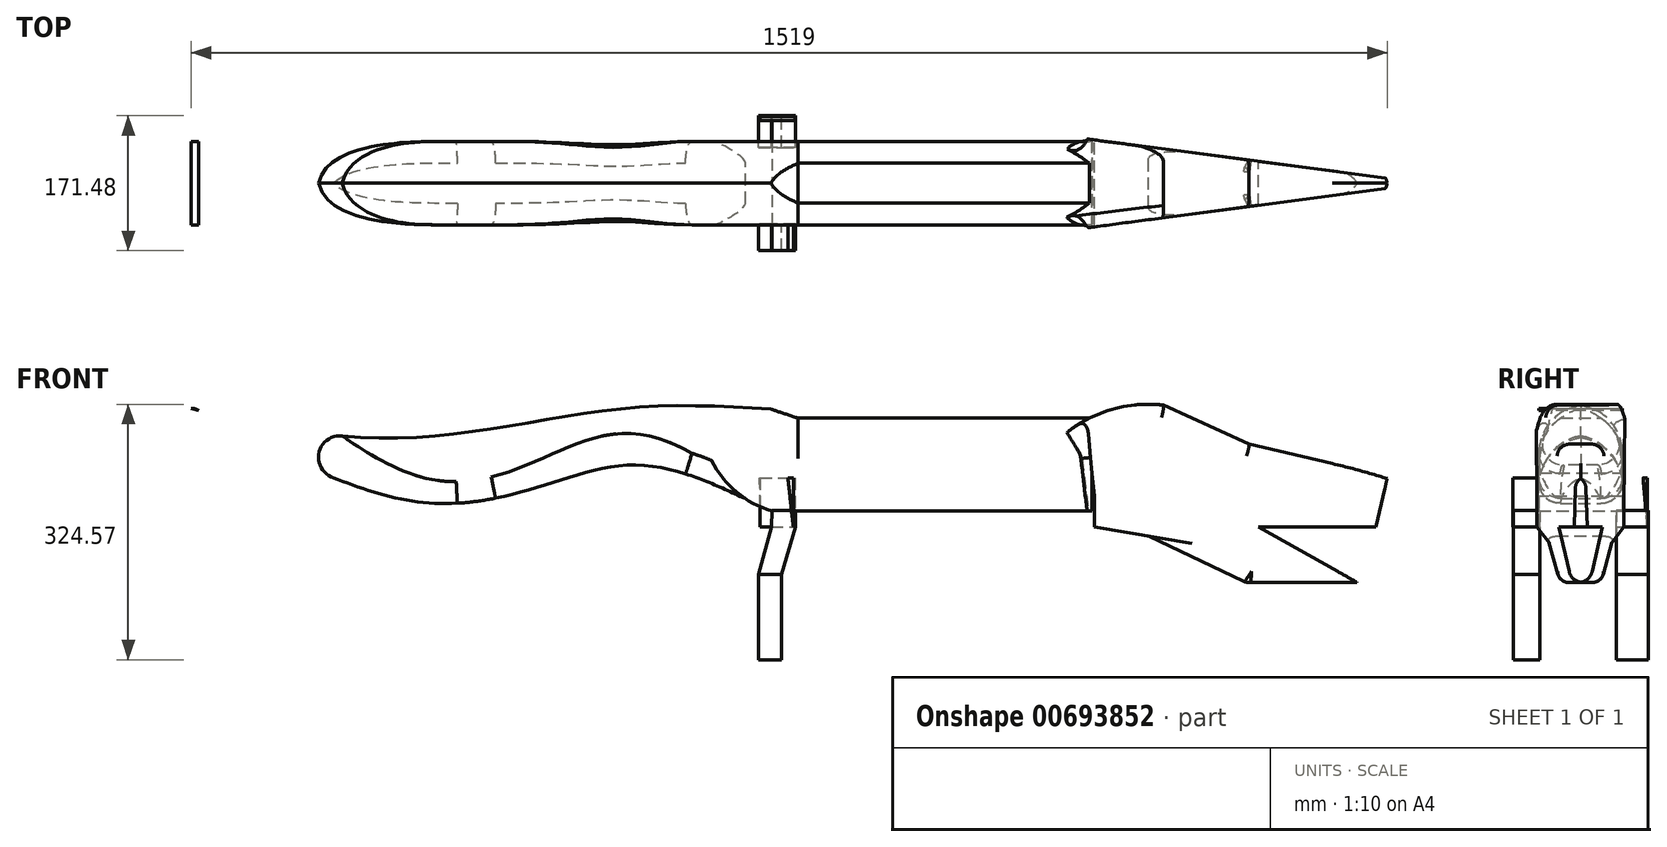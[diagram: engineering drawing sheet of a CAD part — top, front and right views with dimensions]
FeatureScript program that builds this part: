
annotation { "Feature Type Name" : "Feature", "Feature Type Description" : "" }
export const myFeature = defineFeature(function(context is Context, id is Id, definition is map)
    precondition{}
    {
        {
            var Q0;
            Q0=qCreatedBy(makeId("Front.planeOp"),FACE);
            var sketch = newSketch(context, id + "F0", { "sketchPlane" : qUnion([Q0])});
            skLineSegment(sketch, "E0", {"start": v(-53.86, 0) * mm, "end": v(-70.14, -60.07) * mm});
            skLineSegment(sketch, "E1", {"start": v(-70.14, -60.07) * mm, "end": v(-40.72, -60.07) * mm});
            skLineSegment(sketch, "E2", {"start": v(-40.72, -60.07) * mm, "end": v(-23.4, 0) * mm});
            skLineSegment(sketch, "E3", {"start": v(-23.4, 0) * mm, "end": v(27.61, 0) * mm});
            skLineSegment(sketch, "E4", {"start": v(27.61, 0) * mm, "end": v(27.61, -61.63) * mm});
            skLineSegment(sketch, "E5", {"start": v(27.61, -61.63) * mm, "end": v(54.41, -61.63) * mm});
            skLineSegment(sketch, "E6", {"start": v(54.41, -61.63) * mm, "end": v(55.43, 0) * mm});
            skLineSegment(sketch, "E7", {"start": v(55.43, 0) * mm, "end": v(55.8, 22.02) * mm});
            skLineSegment(sketch, "E8", {"start": v(55.8, 22.02) * mm, "end": v(-52.85, 21.34) * mm});
            skLineSegment(sketch, "E9", {"start": v(-52.85, 21.34) * mm, "end": v(-53.86, 0) * mm});
            skSolve(sketch);
        }
        {
            var Q0;
            Q0 = qSketchRegion(id + "F0", true);
            extrude(context, id + "F1", {"entities" : qUnion([Q0]), "endBound" : BoundingType.SYMMETRIC, "depth" : 171.23 * mm, "offsetDistance" : 25.4 * mm});
        }
        {
            var Q0;
            Q0=qCreatedBy(makeId("Right.planeOp"),FACE);
            var sketch = newSketch(context, id + "F2", { "sketchPlane" : qUnion([Q0])});
            skLineSegment(sketch, "E10.bottom", {"start": v(-51.76, 31.02) * mm, "end": v(45.2, 31.02) * mm});
            skLineSegment(sketch, "E10.top", {"start": v(-51.76, -73.58) * mm, "end": v(45.2, -73.58) * mm});
            skLineSegment(sketch, "E10.left", {"start": v(-51.76, 31.02) * mm, "end": v(-51.76, -73.58) * mm});
            skLineSegment(sketch, "E10.right", {"start": v(45.2, 31.02) * mm, "end": v(45.2, -73.58) * mm});
            skSolve(sketch);
        }
        {
            var Q0;
            Q0 = qSketchRegion(id + "F2", true);
            extrude(context, id + "F3", {"entities" : qUnion([Q0]), "operationType" : NewBodyOperationType.REMOVE, "endBound" : BoundingType.SYMMETRIC, "oppositeDirection" : true, "depth" : 377.92 * mm, "offsetDistance" : 25.4 * mm});
        }
        {
            var Q0;
            Q0=qCreatedBy(makeId("Front.planeOp"),FACE);
            var sketch = newSketch(context, id + "F4", { "sketchPlane" : qUnion([Q0])});
            skLineSegment(sketch, "E11.bottom", {"start": v(-23.26, 23.35) * mm, "end": v(61.77, 23.35) * mm});
            skLineSegment(sketch, "E11.top", {"start": v(-23.26, -66.33) * mm, "end": v(61.77, -66.33) * mm});
            skLineSegment(sketch, "E11.left", {"start": v(-23.26, 23.35) * mm, "end": v(-23.26, -66.33) * mm});
            skLineSegment(sketch, "E11.right", {"start": v(61.77, 23.35) * mm, "end": v(61.77, -66.33) * mm});
            skSolve(sketch);
        }
        {
            var Q0;
            Q0=makeQuery(id+"F4.imprint","IMPRINT",FACE,{"disambiguationData":[TD([[makeQuery(id+"F4.imprint","IMPRINT",EDGE,{"derivedFrom":sQuery(id+"F4.wireOp",EDGE,"E11.bottom")}),-1.0]])]});
            extrude(context, id + "F5", {"entities" : qUnion([Q0]), "operationType" : NewBodyOperationType.REMOVE, "endBound" : BoundingType.SYMMETRIC, "depth" : 666.9 * mm, "offsetDistance" : 25.4 * mm});
        }
        {
            var Q0;
            Q0=makeQuery(id+"F4.imprint","IMPRINT",FACE,{"disambiguationData":[TD([[makeQuery(id+"F4.imprint","IMPRINT",EDGE,{"derivedFrom":sQuery(id+"F4.wireOp",EDGE,"E11.bottom")}),-1.0]])]});
            extrude(context, id + "F6", {"entities" : qUnion([Q0]), "operationType" : NewBodyOperationType.REMOVE, "depth" : 410.42 * mm, "offsetDistance" : 25.4 * mm});
        }
        {
            var Q0;
            Q0=qCreatedBy(makeId("Front.planeOp"),FACE);
            var sketch = newSketch(context, id + "F7", { "sketchPlane" : qUnion([Q0])});
            skFitSpline(sketch, "E12", {"points": [v(-86.96, 36.28) * mm, v(-245.8, 78.26) * mm, v(-505.62, 32.65) * mm, v(-786.2, 150.55) * mm, v(-790.65, 150.56) * mm], "startDerivative": vector(-580.58, 269.58) * mm, "endDerivative": vector(-61.42, -29.2) * mm});
            skFitSpline(sketch, "E13", {"points": [v(-790.65, 150.56) * mm, v(-523.28, 113.86) * mm, v(-248.53, 150.56) * mm, v(-56.26, 150.56) * mm], "startDerivative": vector(752.16, -167.95) * mm, "endDerivative": vector(620.07, -38.03) * mm});
            skArc(sketch, "E14", {"start": v(-86.96, 36.28) * mm, "mid": v(-70.22, 27.1) * mm, "end": v(-52.25, 20.62) * mm});
            skLineSegment(sketch, "E15", {"start": v(-56.26, 150.56) * mm, "end": v(-19.94, 138.54) * mm});
            skLineSegment(sketch, "E16", {"start": v(-19.94, 20.62) * mm, "end": v(-19.94, 138.54) * mm});
            skLineSegment(sketch, "E17", {"start": v(-52.25, 20.62) * mm, "end": v(-19.94, 20.62) * mm});
            skSolve(sketch);
        }
        {
            var Q0;
            Q0 = qSketchRegion(id + "F7", true);
            extrude(context, id + "F8", {"entities" : qUnion([Q0]), "endBound" : BoundingType.SYMMETRIC, "depth" : 106.25 * mm, "offsetDistance" : 25.4 * mm});
        }
        {
            var Q0;
            {var subQ0=sQuery(id+"F7.wireOp",EDGE,"E13");Q0=makeQuery(id+"F8.opExtrude","CAP_EDGE",EDGE,{"disambiguationData":[OSD([subQ0]),TDD([makeQuery(id+"F7.imprint","IMPRINT",EDGE,{"disambiguationData":[TD([[makeQuery(id+"F7.imprint","INTERSECT",VERTEX,{"derivedFrom":[subQ0,sQuery(id+"F7.wireOp",EDGE,"E15")]}),1.0]])],"derivedFrom":subQ0})])],"isStart":false});}
            var Q1;
            {var subQ0=sQuery(id+"F7.wireOp",EDGE,"E13");Q1=makeQuery(id+"F8.opExtrude","CAP_EDGE",EDGE,{"disambiguationData":[OSD([subQ0]),TDD([makeQuery(id+"F7.imprint","IMPRINT",EDGE,{"disambiguationData":[TD([[makeQuery(id+"F7.imprint","INTERSECT",VERTEX,{"derivedFrom":[subQ0,sQuery(id+"F7.wireOp",EDGE,"E15")]}),1.0]])],"derivedFrom":subQ0})])],"isStart":true});}
            fillet(context, id + "F9", {"entities" : qUnion([Q0, Q1]), "radius" : 61 * mm, "tangentPropagation" : true, "allowEdgeOverflow" : false});
        }
        {
            var Q0;
            {var subQ0=sQuery(id+"F7.wireOp",EDGE,"E12");Q0=makeQuery(id+"F8.opExtrude","CAP_EDGE",EDGE,{"disambiguationData":[OSD([subQ0]),TDD([makeQuery(id+"F7.imprint","IMPRINT",EDGE,{"disambiguationData":[TD([[makeQuery(id+"F7.imprint","INTERSECT",VERTEX,{"derivedFrom":[subQ0,sQuery(id+"F7.wireOp",EDGE,"E14")]}),-1.0]])],"derivedFrom":subQ0})])],"isStart":false});}
            var Q1;
            {var subQ0=sQuery(id+"F7.wireOp",EDGE,"E12");var subQ1=sQuery(id+"F7.wireOp",EDGE,"E13");Q1=makeQuery(id+"F9.opFillet","BLEND_EDGE",EDGE,{"blendedFrom":[makeQuery(id+"F8.opExtrude","CAP_EDGE",EDGE,{"disambiguationData":[OSD([subQ1]),TDD([makeQuery(id+"F7.imprint","IMPRINT",EDGE,{"disambiguationData":[TD([[makeQuery(id+"F7.imprint","INTERSECT",VERTEX,{"derivedFrom":[subQ1,sQuery(id+"F7.wireOp",EDGE,"E15")]}),1.0]])],"derivedFrom":subQ1})])],"isStart":true}),makeQuery(id+"F8.opExtrude","SWEPT_FACE",FACE,{"disambiguationData":[OSD([subQ0]),TDD([makeQuery(id+"F7.imprint","IMPRINT",EDGE,{"disambiguationData":[TD([[makeQuery(id+"F7.imprint","INTERSECT",VERTEX,{"derivedFrom":[subQ0,sQuery(id+"F7.wireOp",EDGE,"E14")]}),-1.0]])],"derivedFrom":subQ0})])]})],"blendedInto":[makeQuery(id+"F8.opExtrude","SWEPT_FACE",FACE,{"disambiguationData":[OSD([subQ0]),TDD([makeQuery(id+"F7.imprint","IMPRINT",EDGE,{"disambiguationData":[TD([[makeQuery(id+"F7.imprint","INTERSECT",VERTEX,{"derivedFrom":[subQ0,sQuery(id+"F7.wireOp",EDGE,"E14")]}),-1.0]])],"derivedFrom":subQ0})])]})]});}
            fillet(context, id + "F10", {"entities" : qUnion([Q0, Q1]), "radius" : 27.37 * mm, "tangentPropagation" : true, "allowEdgeOverflow" : false});
        }
        {
            var Q0;
            {var subQ2=sQuery(id+"F0.wireOp",EDGE,"E1");Q0=makeQuery(id+"F3.boolean.opBoolean","SPLIT",FACE,{"disambiguationData":[TD([makeQuery(id+"F3.opExtrude","SWEPT_FACE",FACE,{"disambiguationData":[OSD([sQuery(id+"F2.wireOp",EDGE,"E10.left")])]})])],"derivedFrom":makeQuery(id+"F1.opExtrude","SWEPT_FACE",FACE,{"disambiguationData":[OSD([subQ2])]})});}
            var Q1;
            {var subQ2=sQuery(id+"F0.wireOp",EDGE,"E1");Q1=makeQuery(id+"F3.boolean.opBoolean","SPLIT",FACE,{"disambiguationData":[TD([makeQuery(id+"F3.opExtrude","SWEPT_FACE",FACE,{"disambiguationData":[OSD([sQuery(id+"F2.wireOp",EDGE,"E10.right")])]})])],"derivedFrom":makeQuery(id+"F1.opExtrude","SWEPT_FACE",FACE,{"disambiguationData":[OSD([subQ2])]})});}
            extrude(context, id + "F11", {"entities" : qUnion([Q0, Q1]), "depth" : 108.32 * mm, "offsetDistance" : 25.4 * mm});
        }
        {
            var Q0;
            Q0=qCreatedBy(makeId("Top.planeOp"),FACE);
            var sketch = newSketch(context, id + "F12", { "sketchPlane" : qUnion([Q0])});
            skArc(sketch, "E18", {"start": v(-92.58, 54.35) * mm, "mid": v(-75.05, 65.13) * mm, "end": v(-68.29, 84.56) * mm});
            skArc(sketch, "E19", {"start": v(-71.39, -85.85) * mm, "mid": v(-76.16, -65.76) * mm, "end": v(-92.58, -53.25) * mm});
            skLineSegment(sketch, "E20", {"start": v(-68.29, 84.56) * mm, "end": v(-23.93, 84.56) * mm});
            skLineSegment(sketch, "E21", {"start": v(-23.93, 84.56) * mm, "end": v(-23.93, 56.67) * mm});
            skLineSegment(sketch, "E22", {"start": v(-23.93, 56.67) * mm, "end": v(-92.58, 54.35) * mm});
            skLineSegment(sketch, "E23", {"start": v(-92.58, -53.25) * mm, "end": v(-25.76, -53.25) * mm});
            skLineSegment(sketch, "E24", {"start": v(-25.76, -53.25) * mm, "end": v(-25.76, -85.87) * mm});
            skLineSegment(sketch, "E25", {"start": v(-25.76, -85.87) * mm, "end": v(-71.39, -85.85) * mm});
            skSolve(sketch);
        }
        {
            var Q0;
            Q0 = qSketchRegion(id + "F12", true);
            extrude(context, id + "F13", {"entities" : qUnion([Q0]), "depth" : 62.6 * mm, "offsetDistance" : 25.4 * mm});
        }
        {
            var Q0;
            Q0=makeQuery(id+"F8.opExtrude","SWEPT_FACE",FACE,{"disambiguationData":[OSD([sQuery(id+"F7.wireOp",EDGE,"E16")])]});
            extrude(context, id + "F14", {"entities" : qUnion([Q0]), "operationType" : NewBodyOperationType.ADD, "depth" : 373.55 * mm, "offsetDistance" : 25.4 * mm});
        }
        {
            var Q0;
            Q0=qCreatedBy(makeId("Front.planeOp"),FACE);
            var sketch = newSketch(context, id + "F15", { "sketchPlane" : qUnion([Q0])});
            skArc(sketch, "E26", {"start": v(444.04, 155.1) * mm, "mid": v(394.29, 153.32) * mm, "end": v(347.26, 137) * mm});
            skLineSegment(sketch, "E27", {"start": v(444.04, 155.1) * mm, "end": v(552.73, 105.56) * mm});
            skLineSegment(sketch, "E28", {"start": v(552.73, 105.56) * mm, "end": v(729, 64.4) * mm});
            skLineSegment(sketch, "E29", {"start": v(729, 64.4) * mm, "end": v(713.96, 0) * mm});
            skLineSegment(sketch, "E30", {"start": v(713.96, 0) * mm, "end": v(565.16, 0) * mm});
            skLineSegment(sketch, "E31", {"start": v(565.16, 0) * mm, "end": v(690.34, -70.18) * mm});
            skLineSegment(sketch, "E32", {"start": v(690.34, -70.18) * mm, "end": v(549.21, -70.18) * mm});
            skLineSegment(sketch, "E33", {"start": v(549.21, -70.18) * mm, "end": v(425.11, -11.38) * mm});
            skLineSegment(sketch, "E34", {"start": v(425.11, -11.38) * mm, "end": v(356.25, 0) * mm});
            skLineSegment(sketch, "E35", {"start": v(356.25, 0) * mm, "end": v(356.25, 39.66) * mm});
            skLineSegment(sketch, "E36", {"start": v(356.25, 39.66) * mm, "end": v(347.26, 137) * mm});
            skSolve(sketch);
        }
        {
            var Q0;
            Q0 = qSketchRegion(id + "F15", true);
            extrude(context, id + "F16", {"entities" : qUnion([Q0]), "operationType" : NewBodyOperationType.ADD, "endBound" : BoundingType.SYMMETRIC, "depth" : 139.72 * mm, "offsetDistance" : 25.4 * mm});
        }
        {
            var Q0;
            Q0=qCreatedBy(makeId("Top.planeOp"),FACE);
            var sketch = newSketch(context, id + "F17", { "sketchPlane" : qUnion([Q0])});
            skLineSegment(sketch, "E37", {"start": v(345.52, -56.98) * mm, "end": v(777.47, 0) * mm});
            skLineSegment(sketch, "E38", {"start": v(777.47, 0) * mm, "end": v(343.96, 56.5) * mm});
            skLineSegment(sketch, "E39", {"start": v(343.96, 56.5) * mm, "end": v(371.94, 271.16) * mm});
            skLineSegment(sketch, "E40", {"start": v(371.94, 271.16) * mm, "end": v(821.7, 200.38) * mm});
            skLineSegment(sketch, "E41", {"start": v(821.7, 200.38) * mm, "end": v(777.47, 0) * mm});
            skLineSegment(sketch, "E42", {"start": v(777.47, 0) * mm, "end": v(845.32, -168.96) * mm});
            skLineSegment(sketch, "E43", {"start": v(845.32, -168.96) * mm, "end": v(351.41, -145.9) * mm});
            skLineSegment(sketch, "E44", {"start": v(351.41, -145.9) * mm, "end": v(345.52, -56.98) * mm});
            skSolve(sketch);
        }
        {
            var Q0;
            Q0=makeQuery(id+"F17.imprint","IMPRINT",FACE,{"disambiguationData":[TD([[makeQuery(id+"F17.imprint","IMPRINT",EDGE,{"derivedFrom":sQuery(id+"F17.wireOp",EDGE,"E37")}),-1.0]])]});
            var Q1;
            Q1=makeQuery(id+"F17.imprint","IMPRINT",FACE,{"disambiguationData":[TD([[makeQuery(id+"F17.imprint","IMPRINT",EDGE,{"derivedFrom":sQuery(id+"F17.wireOp",EDGE,"E38")}),-1.0]])]});
            extrude(context, id + "F18", {"entities" : qUnion([Q0, Q1]), "operationType" : NewBodyOperationType.REMOVE, "endBound" : BoundingType.SYMMETRIC, "depth" : 503.6 * mm, "offsetDistance" : 25.4 * mm});
        }
        {
            var Q0;
            Q0=makeQuery(id+"F18.boolean.opBoolean","INTERSECT",EDGE,{"derivedFrom":[makeQuery(id+"F16.opExtrude","SWEPT_FACE",FACE,{"disambiguationData":[OSD([sQuery(id+"F15.wireOp",EDGE,"E28")])]}),makeQuery(id+"F18.opExtrude","SWEPT_FACE",FACE,{"disambiguationData":[OSD([sQuery(id+"F17.wireOp",EDGE,"E37")])]})]});
            var Q1;
            Q1=makeQuery(id+"F18.boolean.opBoolean","INTERSECT",EDGE,{"derivedFrom":[makeQuery(id+"F16.opExtrude","SWEPT_FACE",FACE,{"disambiguationData":[OSD([sQuery(id+"F15.wireOp",EDGE,"E28")])]}),makeQuery(id+"F18.opExtrude","SWEPT_FACE",FACE,{"disambiguationData":[OSD([sQuery(id+"F17.wireOp",EDGE,"E38")])]})]});
            var Q2;
            Q2=makeQuery(id+"F18.boolean.opBoolean","INTERSECT",EDGE,{"derivedFrom":[makeQuery(id+"F16.opExtrude","SWEPT_FACE",FACE,{"disambiguationData":[OSD([sQuery(id+"F15.wireOp",EDGE,"E27")])]}),makeQuery(id+"F18.opExtrude","SWEPT_FACE",FACE,{"disambiguationData":[OSD([sQuery(id+"F17.wireOp",EDGE,"E37")])]})]});
            var Q3;
            Q3=makeQuery(id+"F18.boolean.opBoolean","INTERSECT",EDGE,{"derivedFrom":[makeQuery(id+"F16.opExtrude","SWEPT_FACE",FACE,{"disambiguationData":[OSD([sQuery(id+"F15.wireOp",EDGE,"E27")])]}),makeQuery(id+"F18.opExtrude","SWEPT_FACE",FACE,{"disambiguationData":[OSD([sQuery(id+"F17.wireOp",EDGE,"E38")])]})]});
            var Q4;
            Q4=makeQuery(id+"F18.boolean.opBoolean","INTERSECT",EDGE,{"derivedFrom":[makeQuery(id+"F16.opExtrude","SWEPT_FACE",FACE,{"disambiguationData":[OSD([sQuery(id+"F15.wireOp",EDGE,"E26")])]}),makeQuery(id+"F18.opExtrude","SWEPT_FACE",FACE,{"disambiguationData":[OSD([sQuery(id+"F17.wireOp",EDGE,"E37")])]})]});
            fillet(context, id + "F19", {"entities" : qUnion([Q0, Q1, Q2, Q3, Q4]), "radius" : 15.87 * mm, "tangentPropagation" : true, "allowEdgeOverflow" : false});
        }
        {
            var Q0;
            {var subQ0=sQuery(id+"F7.wireOp",EDGE,"E16");var subQ1=sQuery(id+"F7.wireOp",EDGE,"E13");Q0=makeQuery(id+"F16.boolean.opBoolean","INTERSECT",EDGE,{"derivedFrom":[makeQuery(id+"F14.opExtrude","SWEPT_FACE",FACE,{"disambiguationData":[OSD([subQ1,subQ0]),TDD([makeQuery(id+"F9.opFillet","BLEND_EDGE",EDGE,{"blendedFrom":[makeQuery(id+"F8.opExtrude","CAP_EDGE",EDGE,{"disambiguationData":[OSD([subQ1]),TDD([makeQuery(id+"F7.imprint","IMPRINT",EDGE,{"disambiguationData":[TD([[makeQuery(id+"F7.imprint","INTERSECT",VERTEX,{"derivedFrom":[subQ1,sQuery(id+"F7.wireOp",EDGE,"E15")]}),1.0]])],"derivedFrom":subQ1})])],"isStart":false}),makeQuery(id+"F8.opExtrude","SWEPT_FACE",FACE,{"disambiguationData":[OSD([subQ0])]})],"blendedInto":[makeQuery(id+"F8.opExtrude","SWEPT_FACE",FACE,{"disambiguationData":[OSD([subQ0])]})]})])]}),makeQuery(id+"F16.opExtrude","SWEPT_FACE",FACE,{"disambiguationData":[OSD([sQuery(id+"F15.wireOp",EDGE,"E36")])]})]});}
            var Q1;
            {var subQ0=sQuery(id+"F7.wireOp",EDGE,"E16");var subQ1=sQuery(id+"F7.wireOp",EDGE,"E13");Q1=makeQuery(id+"F16.boolean.opBoolean","INTERSECT",EDGE,{"derivedFrom":[makeQuery(id+"F14.opExtrude","SWEPT_FACE",FACE,{"disambiguationData":[OSD([subQ1,subQ0]),TDD([makeQuery(id+"F9.opFillet","BLEND_EDGE",EDGE,{"blendedFrom":[makeQuery(id+"F8.opExtrude","CAP_EDGE",EDGE,{"disambiguationData":[OSD([subQ1]),TDD([makeQuery(id+"F7.imprint","IMPRINT",EDGE,{"disambiguationData":[TD([[makeQuery(id+"F7.imprint","INTERSECT",VERTEX,{"derivedFrom":[subQ1,sQuery(id+"F7.wireOp",EDGE,"E15")]}),1.0]])],"derivedFrom":subQ1})])],"isStart":true}),makeQuery(id+"F8.opExtrude","SWEPT_FACE",FACE,{"disambiguationData":[OSD([subQ0])]})],"blendedInto":[makeQuery(id+"F8.opExtrude","SWEPT_FACE",FACE,{"disambiguationData":[OSD([subQ0])]})]})])]}),makeQuery(id+"F16.opExtrude","SWEPT_FACE",FACE,{"disambiguationData":[OSD([sQuery(id+"F15.wireOp",EDGE,"E36")])]})]});}
            fillet(context, id + "F20", {"entities" : qUnion([Q0, Q1]), "radius" : 27.18 * mm, "tangentPropagation" : true, "allowEdgeOverflow" : false});
        }
        {
            var Q0;
            Q0=makeQuery(id+"F18.boolean.opBoolean","INTERSECT",EDGE,{"derivedFrom":[makeQuery(id+"F16.opExtrude","SWEPT_FACE",FACE,{"disambiguationData":[OSD([sQuery(id+"F15.wireOp",EDGE,"E32")])]}),makeQuery(id+"F18.opExtrude","SWEPT_FACE",FACE,{"disambiguationData":[OSD([sQuery(id+"F17.wireOp",EDGE,"E37")])]})]});
            var Q1;
            Q1=makeQuery(id+"F18.boolean.opBoolean","INTERSECT",EDGE,{"derivedFrom":[makeQuery(id+"F16.opExtrude","SWEPT_FACE",FACE,{"disambiguationData":[OSD([sQuery(id+"F15.wireOp",EDGE,"E32")])]}),makeQuery(id+"F18.opExtrude","SWEPT_FACE",FACE,{"disambiguationData":[OSD([sQuery(id+"F17.wireOp",EDGE,"E38")])]})]});
            fillet(context, id + "F21", {"entities" : qUnion([Q0, Q1]), "radius" : 13.8 * mm, "tangentPropagation" : true, "allowEdgeOverflow" : false});
        }
        {
            var Q0;
            Q0=makeQuery(id+"F16.opExtrude","SWEPT_EDGE",EDGE,{"disambiguationData":[OSD([sQuery(id+"F15.wireOp",EDGE,"E32"),sQuery(id+"F15.wireOp",EDGE,"E33")])]});
            fillet(context, id + "F22", {"entities" : qUnion([Q0]), "radius" : 14.54 * mm, "tangentPropagation" : true, "allowEdgeOverflow" : false});
        }
        {
            var Q0;
            Q0=makeQuery(id+"F13.opExtrude","CAP_EDGE",EDGE,{"disambiguationData":[OSD([sQuery(id+"F12.wireOp",EDGE,"E19")])],"isStart":true});
            var Q1;
            Q1=makeQuery(id+"F13.opExtrude","CAP_EDGE",EDGE,{"disambiguationData":[OSD([sQuery(id+"F12.wireOp",EDGE,"E22")])],"isStart":true});
            var Q2;
            {var subQ2=sQuery(id+"F0.wireOp",EDGE,"E0");Q2=makeQuery(id+"F3.boolean.opBoolean","SPLIT",FACE,{"disambiguationData":[TD([makeQuery(id+"F3.opExtrude","SWEPT_FACE",FACE,{"disambiguationData":[OSD([sQuery(id+"F2.wireOp",EDGE,"E10.right")])]})])],"derivedFrom":makeQuery(id+"F1.opExtrude","SWEPT_FACE",FACE,{"disambiguationData":[OSD([subQ2])]})});}
            var Q3;
            {var subQ0=sQuery(id+"F0.wireOp",EDGE,"E0");var subQ1=sQuery(id+"F0.wireOp",EDGE,"E9");Q3=makeQuery(id+"F3.boolean.opBoolean","SPLIT",EDGE,{"disambiguationData":[TD([makeQuery(id+"F3.opExtrude","SWEPT_FACE",FACE,{"disambiguationData":[OSD([sQuery(id+"F2.wireOp",EDGE,"E10.right")])]})])],"derivedFrom":makeQuery(id+"F1.opExtrude","SWEPT_EDGE",EDGE,{"disambiguationData":[OSD([subQ0,subQ1])]})});}
            fillet(context, id + "F23", {"entities" : qUnion([Q0, Q1, Q2, Q3]), "radius" : 6578.08 * mm, "tangentPropagation" : true, "allowEdgeOverflow" : false});
        }
    });
